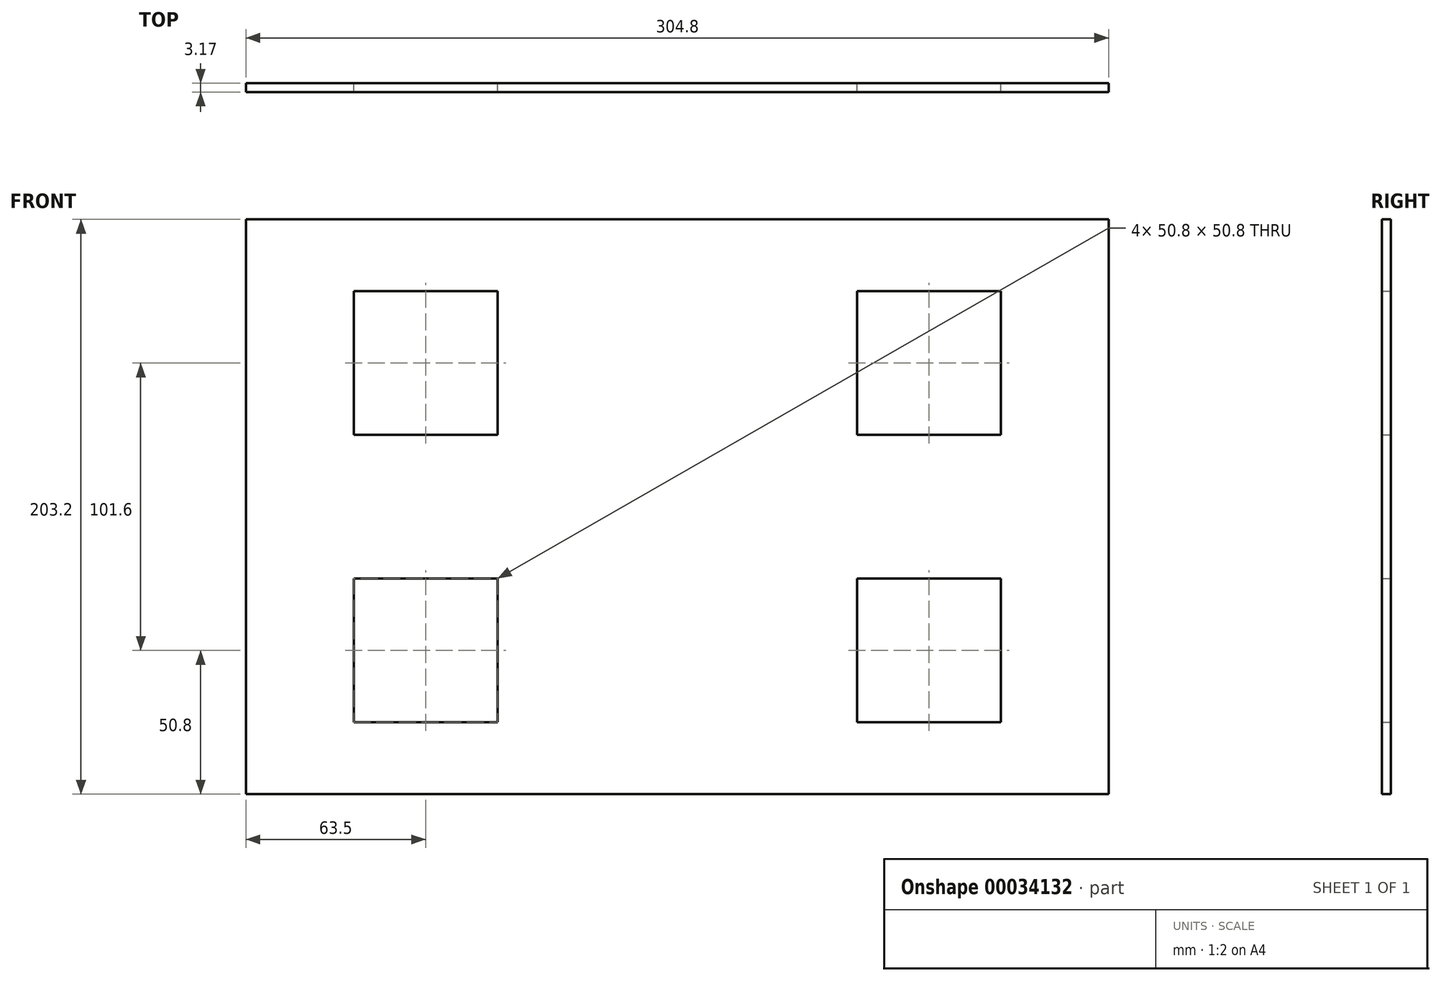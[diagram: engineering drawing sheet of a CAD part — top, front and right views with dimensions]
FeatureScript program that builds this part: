
annotation { "Feature Type Name" : "Feature", "Feature Type Description" : "" }
export const myFeature = defineFeature(function(context is Context, id is Id, definition is map)
    precondition{}
    {
        {
            var Q0;
            Q0=qCreatedBy(makeId("Front.planeOp"),FACE);
            var sketch = newSketch(context, id + "F0", { "sketchPlane" : qUnion([Q0])});
            skLineSegment(sketch, "E0.rect.bottom", {"start": v(152.4, 101.6) * mm, "end": v(-152.4, 101.6) * mm});
            skLineSegment(sketch, "E0.rect.top", {"start": v(152.4, -101.6) * mm, "end": v(-152.4, -101.6) * mm});
            skLineSegment(sketch, "E0.rect.left", {"start": v(152.4, 101.6) * mm, "end": v(152.4, -101.6) * mm});
            skLineSegment(sketch, "E0.rect.right", {"start": v(-152.4, 101.6) * mm, "end": v(-152.4, -101.6) * mm});
            skPoint(sketch, "E0.rect.middle", {"position": v(0, 0) * mm});
            skLineSegment(sketch, "E1.rect.bottom", {"start": v(-63.5, 76.2) * mm, "end": v(-114.3, 76.2) * mm});
            skLineSegment(sketch, "E1.rect.top", {"start": v(-63.5, 25.4) * mm, "end": v(-114.3, 25.4) * mm});
            skLineSegment(sketch, "E1.rect.left", {"start": v(-63.5, 76.2) * mm, "end": v(-63.5, 25.4) * mm});
            skLineSegment(sketch, "E1.rect.right", {"start": v(-114.3, 76.2) * mm, "end": v(-114.3, 25.4) * mm});
            skPoint(sketch, "E1.rect.middle", {"position": v(-88.9, 50.8) * mm});
            skLineSegment(sketch, "E2.rect.bottom", {"start": v(114.3, 76.2) * mm, "end": v(63.5, 76.2) * mm});
            skLineSegment(sketch, "E2.rect.top", {"start": v(114.3, 25.4) * mm, "end": v(63.5, 25.4) * mm});
            skLineSegment(sketch, "E2.rect.left", {"start": v(114.3, 76.2) * mm, "end": v(114.3, 25.4) * mm});
            skLineSegment(sketch, "E2.rect.right", {"start": v(63.5, 76.2) * mm, "end": v(63.5, 25.4) * mm});
            skPoint(sketch, "E2.rect.middle", {"position": v(88.9, 50.8) * mm});
            skLineSegment(sketch, "E3.rect.bottom", {"start": v(114.3, -25.4) * mm, "end": v(63.5, -25.4) * mm});
            skLineSegment(sketch, "E3.rect.top", {"start": v(114.3, -76.2) * mm, "end": v(63.5, -76.2) * mm});
            skLineSegment(sketch, "E3.rect.left", {"start": v(114.3, -25.4) * mm, "end": v(114.3, -76.2) * mm});
            skLineSegment(sketch, "E3.rect.right", {"start": v(63.5, -25.4) * mm, "end": v(63.5, -76.2) * mm});
            skPoint(sketch, "E3.rect.middle", {"position": v(88.9, -50.8) * mm});
            skLineSegment(sketch, "E4.rect.bottom", {"start": v(-63.5, -25.4) * mm, "end": v(-114.3, -25.4) * mm});
            skLineSegment(sketch, "E4.rect.top", {"start": v(-63.5, -76.2) * mm, "end": v(-114.3, -76.2) * mm});
            skLineSegment(sketch, "E4.rect.left", {"start": v(-63.5, -25.4) * mm, "end": v(-63.5, -76.2) * mm});
            skLineSegment(sketch, "E4.rect.right", {"start": v(-114.3, -25.4) * mm, "end": v(-114.3, -76.2) * mm});
            skPoint(sketch, "E4.rect.middle", {"position": v(-88.9, -50.8) * mm});
            skLineSegment(sketch, "E5", {"start": v(-88.9, 50.8) * mm, "end": v(-88.9, -50.8) * mm, "construction": true});
            skLineSegment(sketch, "E6", {"start": v(-88.9, -50.8) * mm, "end": v(88.9, -50.8) * mm, "construction": true});
            skLineSegment(sketch, "E7", {"start": v(88.9, 50.8) * mm, "end": v(-88.9, 50.8) * mm, "construction": true});
            skLineSegment(sketch, "E8", {"start": v(88.9, -50.8) * mm, "end": v(88.9, 50.8) * mm, "construction": true});
            skLineSegment(sketch, "E9", {"start": v(0, 50.8) * mm, "end": v(0, 0) * mm, "construction": true});
            skLineSegment(sketch, "E10", {"start": v(0, 50.8) * mm, "end": v(0, 101.6) * mm});
            skLineSegment(sketch, "E11", {"start": v(0, -50.8) * mm, "end": v(0, -101.6) * mm});
            skLineSegment(sketch, "E12", {"start": v(-88.9, 0) * mm, "end": v(-152.4, 0) * mm});
            skLineSegment(sketch, "E13", {"start": v(88.9, 0) * mm, "end": v(152.4, 0) * mm});
            skSolve(sketch);
        }
        {
            var Q0;
            Q0=makeQuery(id+"F0.imprint","IMPRINT",FACE,{"disambiguationData":[TD([[makeQuery(id+"F0.imprint","IMPRINT",EDGE,{"derivedFrom":sQuery(id+"F0.wireOp",EDGE,"E1.rect.bottom")}),-1.0]])]});
            extrude(context, id + "F1", {"entities" : qUnion([Q0]), "depth" : 3.17 * mm});
        }
    });
